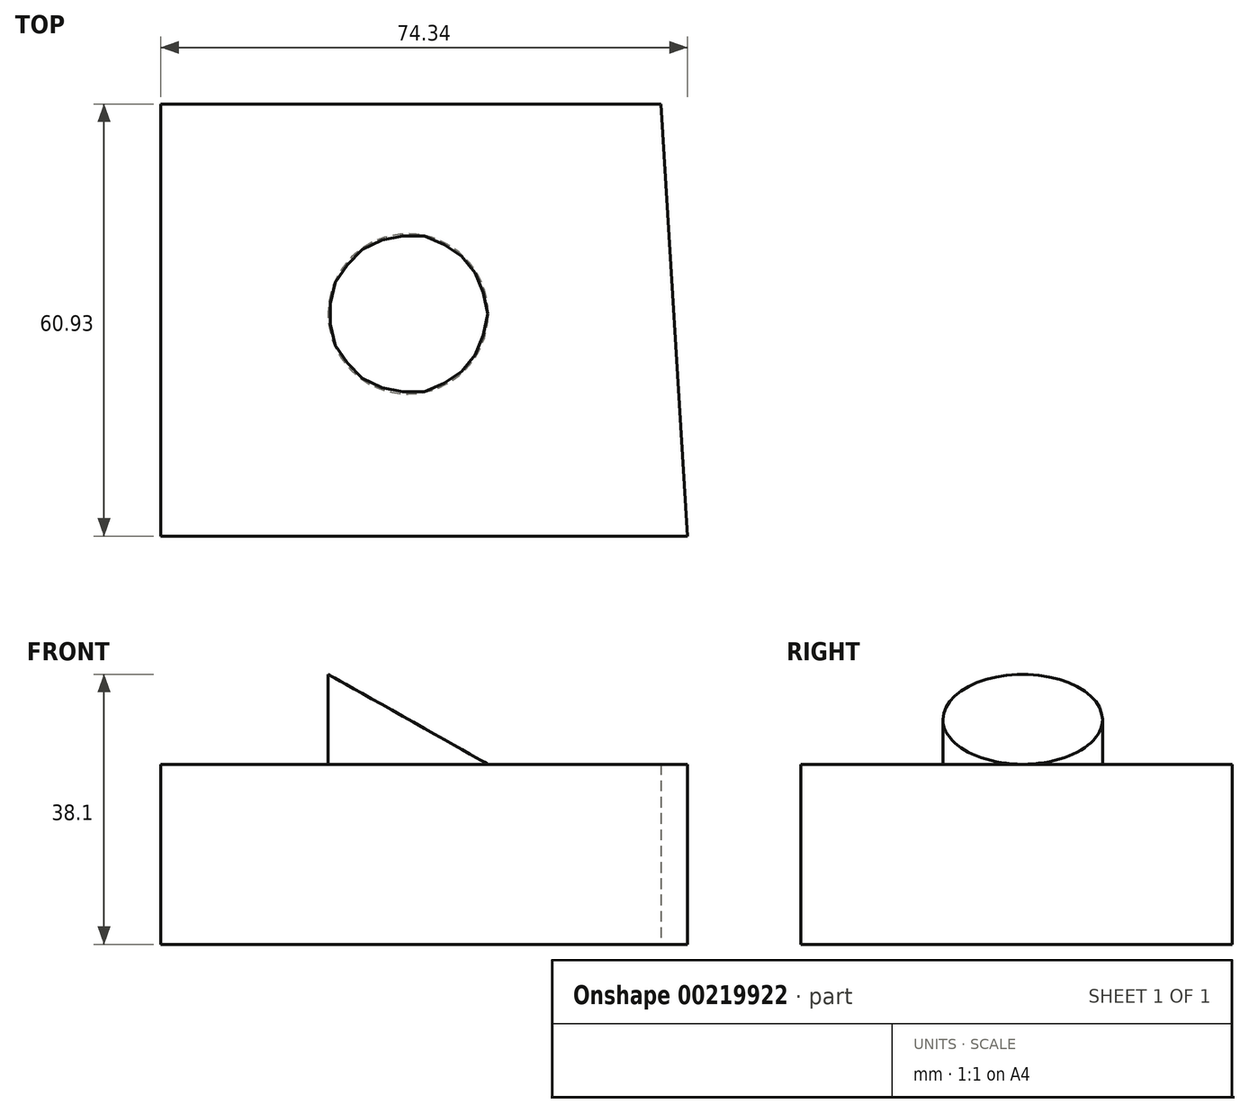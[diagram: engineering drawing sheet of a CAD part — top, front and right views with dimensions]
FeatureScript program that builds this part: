
annotation { "Feature Type Name" : "Feature", "Feature Type Description" : "" }
export const myFeature = defineFeature(function(context is Context, id is Id, definition is map)
    precondition{}
    {
        {
            var Q0;
            Q0=qCreatedBy(makeId("Top.planeOp"),FACE);
            var sketch = newSketch(context, id + "F0", { "sketchPlane" : qUnion([Q0])});
            skLineSegment(sketch, "E0", {"start": v(-44.22, -40.57) * mm, "end": v(30.12, -40.57) * mm});
            skLineSegment(sketch, "E1", {"start": v(-44.22, -40.57) * mm, "end": v(-44.22, 20.36) * mm});
            skLineSegment(sketch, "E2", {"start": v(30.12, -40.57) * mm, "end": v(26.4, 20.36) * mm});
            skLineSegment(sketch, "E3", {"start": v(26.4, 20.36) * mm, "end": v(-44.22, 20.36) * mm});
            skSolve(sketch);
        }
        {
            var Q0;
            Q0 = qSketchRegion(id + "F0", true);
            extrude(context, id + "F1", {"entities" : qUnion([Q0]), "depth" : 25.4 * mm});
        }
        {
            var Q0;
            Q0=makeQuery(id+"F1.opExtrude","CAP_FACE",FACE,{"disambiguationData":[OSD([sQuery(id+"F0.wireOp",EDGE,"E0"),sQuery(id+"F0.wireOp",EDGE,"E1"),sQuery(id+"F0.wireOp",EDGE,"E2"),sQuery(id+"F0.wireOp",EDGE,"E3")])],"isStart":false});
            var sketch = newSketch(context, id + "F2", { "sketchPlane" : qUnion([Q0])});
            skCircle(sketch, "E4", {"center": v(-9.32, -9.23) * mm, "radius": 11.29 * mm});
            skSolve(sketch);
        }
        {
            var Q0;
            Q0 = qSketchRegion(id + "F2", true);
            extrude(context, id + "F3", {"entities" : qUnion([Q0]), "operationType" : NewBodyOperationType.ADD, "depth" : 12.7 * mm});
        }
        {
            var Q0;
            Q0=makeQuery(id+"F1.opExtrude","SWEPT_FACE",FACE,{"disambiguationData":[OSD([sQuery(id+"F0.wireOp",EDGE,"E0")])]});
            var sketch = newSketch(context, id + "F4", { "sketchPlane" : qUnion([Q0])});
            skLineSegment(sketch, "E5.0", {"start": v(-20.6, 38.1) * mm, "end": v(1.97, 38.1) * mm});
            skLineSegment(sketch, "E6", {"start": v(1.97, 38.1) * mm, "end": v(1.97, 25.4) * mm});
            skLineSegment(sketch, "E7", {"start": v(1.97, 25.4) * mm, "end": v(-20.6, 38.1) * mm});
            skSolve(sketch);
        }
        {
            var Q0;
            Q0 = qSketchRegion(id + "F4", true);
            extrude(context, id + "F5", {"entities" : qUnion([Q0]), "operationType" : NewBodyOperationType.REMOVE, "endBound" : BoundingType.THROUGH_ALL, "oppositeDirection" : true, "depth" : 25.4 * mm});
        }
    });
